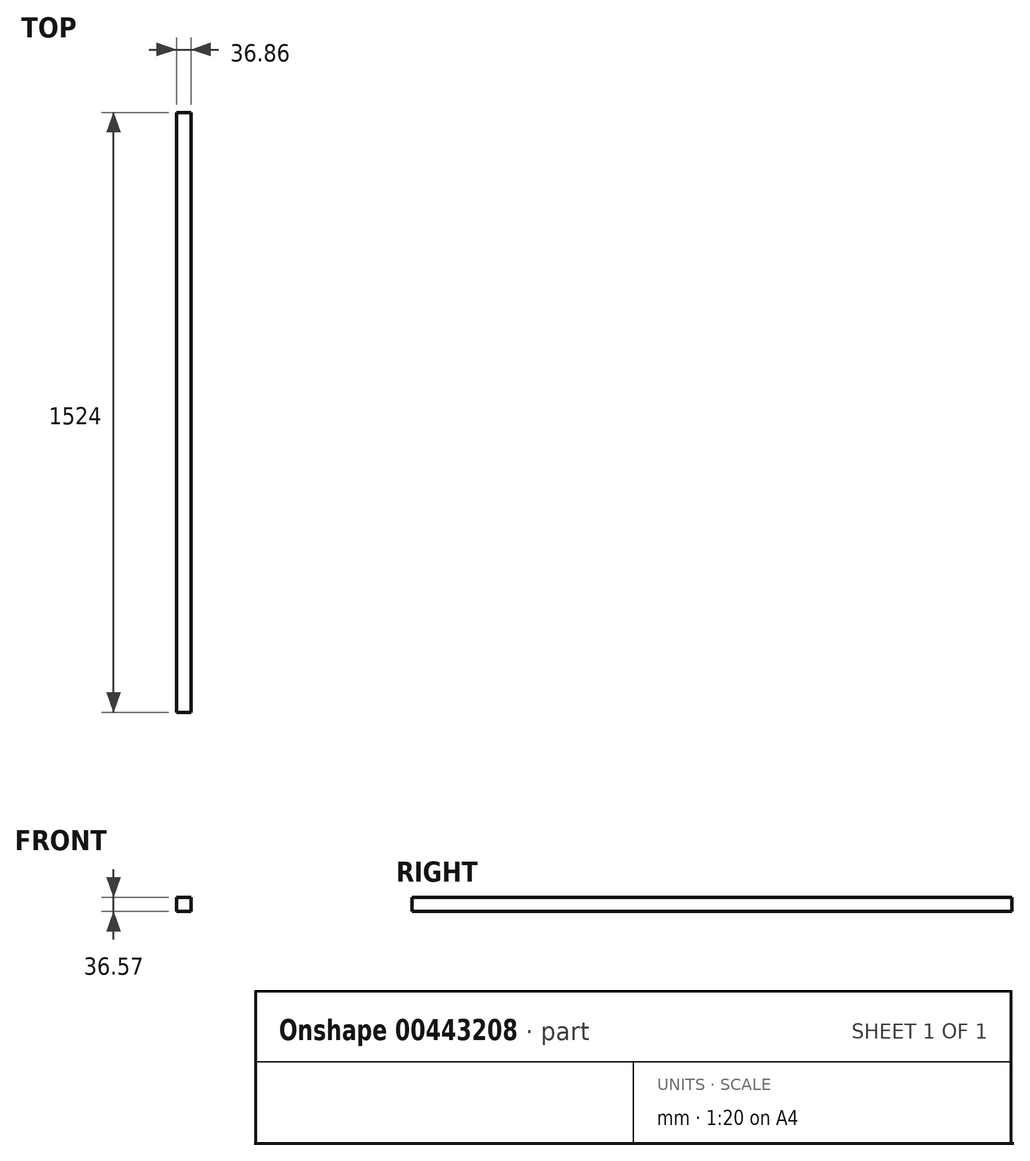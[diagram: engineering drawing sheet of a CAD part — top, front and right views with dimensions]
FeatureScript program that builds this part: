
annotation { "Feature Type Name" : "Feature", "Feature Type Description" : "" }
export const myFeature = defineFeature(function(context is Context, id is Id, definition is map)
    precondition{}
    {
        {
            var Q0;
            Q0=qCreatedBy(makeId("Front.planeOp"),FACE);
            var sketch = newSketch(context, id + "F0", { "sketchPlane" : qUnion([Q0])});
            skLineSegment(sketch, "E0.bottom", {"start": v(-36.86, 36.57) * mm, "end": v(0, 36.57) * mm});
            skLineSegment(sketch, "E0.top", {"start": v(-36.86, 0) * mm, "end": v(0, 0) * mm});
            skLineSegment(sketch, "E0.left", {"start": v(-36.86, 36.57) * mm, "end": v(-36.86, 0) * mm});
            skLineSegment(sketch, "E0.right", {"start": v(0, 36.57) * mm, "end": v(0, 0) * mm});
            skSolve(sketch);
        }
        {
            var Q0;
            Q0=sQuery(id+"F0.wireOp",EDGE,"E0.bottom");
            var Q1;
            Q1=sQuery(id+"F0.wireOp",EDGE,"E0.left");
            var Q2;
            Q2=sQuery(id+"F0.wireOp",EDGE,"E0.top");
            var Q3;
            Q3=sQuery(id+"F0.wireOp",EDGE,"E0.right");
            extrude(context, id + "F1", {"bodyType" : ToolBodyType.SURFACE, "surfaceEntities" : qUnion([Q0, Q1, Q2, Q3]), "depth" : 1524 * mm});
        }
    });
